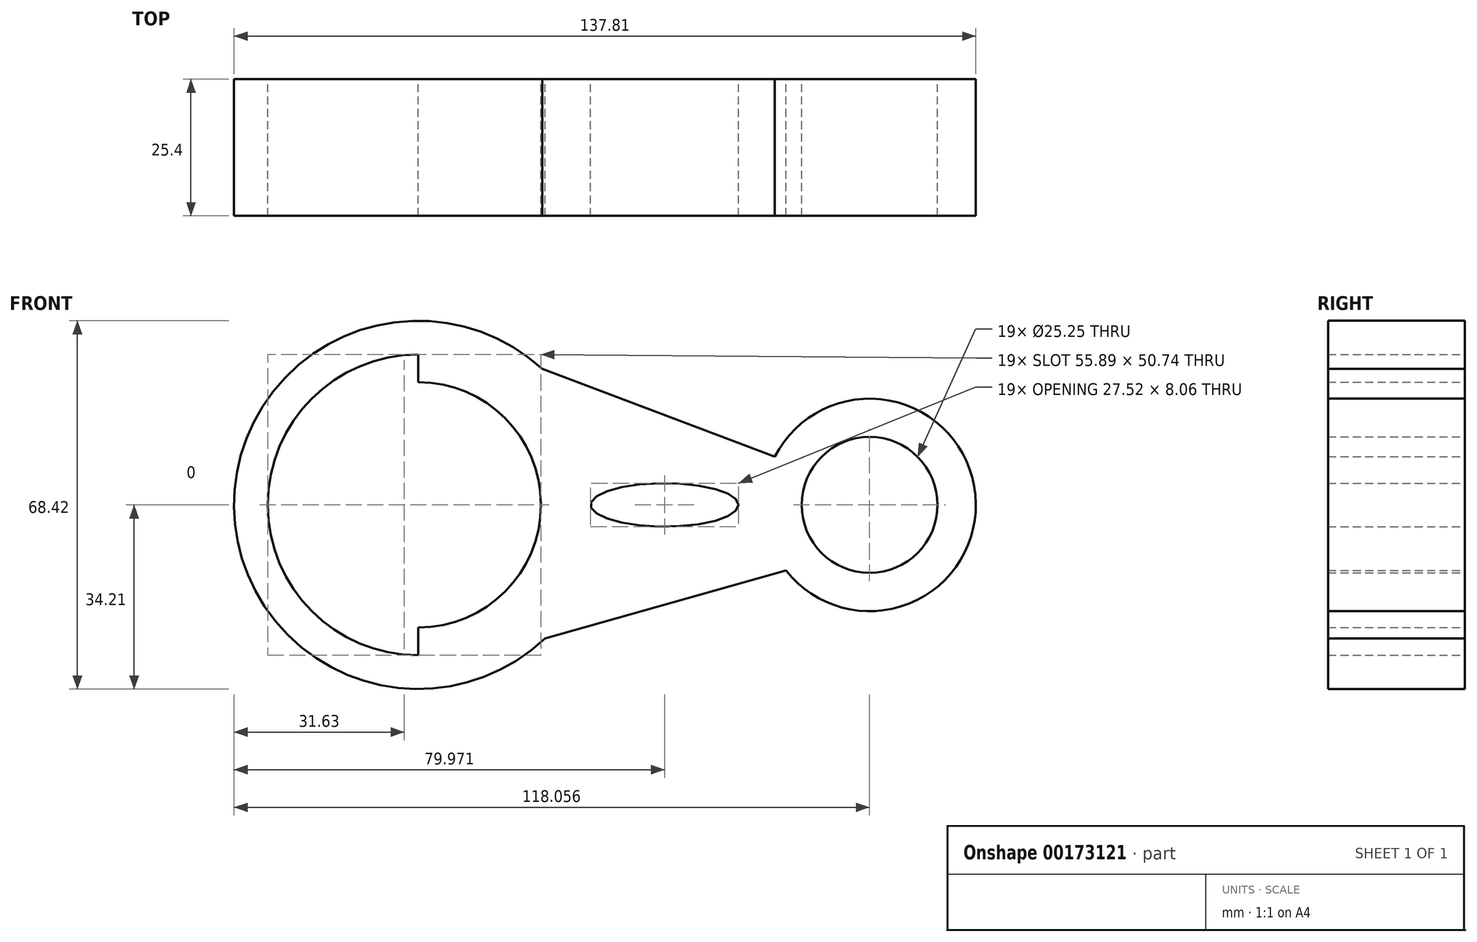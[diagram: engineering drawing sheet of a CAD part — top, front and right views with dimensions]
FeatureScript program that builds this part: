
annotation { "Feature Type Name" : "Feature", "Feature Type Description" : "" }
export const myFeature = defineFeature(function(context is Context, id is Id, definition is map)
    precondition{}
    {
        {
            var Q0;
            Q0=qCreatedBy(makeId("Front.planeOp"),FACE);
            var sketch = newSketch(context, id + "F0", { "sketchPlane" : qUnion([Q0])});
            skCircle(sketch, "E0", {"center": v(-34.56, 0) * mm, "radius": 22.8 * mm});
            skCircle(sketch, "E1", {"center": v(49.29, 0) * mm, "radius": 12.63 * mm});
            skLineSegment(sketch, "E2", {"start": v(-34.56, 46.72) * mm, "end": v(-34.56, -45.77) * mm});
            skPoint(sketch, "E3", {"position": v(-34.56, 46.72) * mm});
            skPoint(sketch, "E4", {"position": v(-34.56, -45.77) * mm});
            skArc(sketch, "E5", {"start": v(-11.52, 25.28) * mm, "mid": v(-68.77, -0.34) * mm, "end": v(-11.02, -24.81) * mm});
            skArc(sketch, "E6", {"start": v(31.68, 8.96) * mm, "mid": v(68.94, 1.93) * mm, "end": v(33.76, -12.2) * mm});
            skLineSegment(sketch, "E7", {"start": v(-11.52, 25.28) * mm, "end": v(31.68, 8.96) * mm});
            skLineSegment(sketch, "E8", {"start": v(-11.02, -24.81) * mm, "end": v(33.76, -12.2) * mm});
            skArc(sketch, "E9", {"start": v(35.52, 8.32) * mm, "mid": v(65.36, 0.57) * mm, "end": v(36.15, -9.28) * mm});
            skArc(sketch, "E10", {"start": v(-16.64, 21.44) * mm, "mid": v(-62.5, -0.92) * mm, "end": v(-15.27, -20.22) * mm});
            skLineSegment(sketch, "E11", {"start": v(-16.64, 21.44) * mm, "end": v(32.96, 4.8) * mm});
            skLineSegment(sketch, "E12", {"start": v(-15.68, -20.48) * mm, "end": v(32.64, -6.72) * mm});
            skLineSegment(sketch, "E13", {"start": v(32.96, 4.8) * mm, "end": v(35.52, 8.32) * mm});
            skLineSegment(sketch, "E14", {"start": v(32.32, -7.04) * mm, "end": v(36.15, -9.28) * mm});
            skEllipse(sketch, "E15", {"center": v(11.2, 0) * mm, "majorRadius": 13.76 * mm, "minorRadius": 4.03 * mm, "majorAxis": v(1, 0)});
            skSolve(sketch);
        }
        {
            var Q0;
            Q0 = qSketchRegion(id + "F0", true);
            extrude(context, id + "F1", {"entities" : qUnion([Q0]), "depth" : 25.4 * mm});
        }
    });
